# Revit family: Gira_212800
name_source: partatom
category: Elektroinstallationen
revit_build: Autodesk Revit 2017 (Build: 20160225_1515(x64)
units: mm (PartAtom-declared; Revit-internal decimal feet)

## family parameters
Basisbauteil = Fläche
Beim Laden mit Abzugskörper schneiden = Nein
Bemaßung runder Anschluss = Durchmesser verwenden
Beschriftungsausrichtung beibehalten = Nein
Gemeinsam genutzt = Nein
Raumberechnungspunkt = Nein
Teiletyp = Normal

## types (1)
- Binäreing. 8f 12 - 48 V AC/DC pot.frei KNX REG
    Anzahl der Ausgänge = 0
    Anzahl der binären Eingänge = 0
    BIM = https://media.stage.bim.site 8f.rfa
    BIMSITE_PRODUCT_ID = 7bffefd257eabbc41457cb73de1d5ba235a54360
    Beschreibung = KNX Binäreingang 8fach 12 - 48 V AC DC potenzialfrei  REG plus REG-Binäreingänge zum Anschluss von Kontakten. Die Schaltvorgänge von Kontakten (z. B. Wächter bzw. Taster) werden in KNX Telegramme umgesetzt. Die Eingänge können dabei unabhängig voneinander verschiedenen Funktionen zugeordnet oder gesperrt werden. Signalanzeige über gelbe Status-LED möglich.  Merkmale:  Jeder Eingang verfügt über den vollen Funktionsumfang. Alle kanalorientierten Funktionen lassen sich separat für jeden Eingang parametrieren.  Aktiv sendende Telegramme der Eingänge lassen sich nach Busspannungswiederkehr oder nach einem ETS-Programmiervorgang global verzögern.  Entprellzeit und Telegrammratenbegrenzung konfigurierbar.  Freie Zuordnung der Funktionen Schalten, Dimmen, Jalousie, Wertgeber und Impulszähler zu den Eingängen.  Sperrobjekt zum Sperren einzelner Eingänge (Polarität des Sperrobjekts einstellbar) für die Funktionen Schalten, Dimmen, Jalousie und Wertgeber.  Verhalten bei Busspannungswiederkehr für jeden Eingang separat parametrierbar.  Funktion Schalten: zwei unabhängige Schaltobjekte für jeden Eingang vorhanden (Schaltbefehle sind einzeln parametrierbar), Befehl bei steigender und fallender Flanke unabhängig einstellbar (EIN, AUS, UM, keine Reaktion), unabhängiges zyklisches Senden der Schaltobjekte in Abhängigkeit der Flanke oder in Abhängigkeit des Objektwerts wählbar.  Funktion Dimmen: Einflächen- und Zweiflächenbedienung, Zeit zwischen Dimmen und Schalten und Dimmschrittweite einstellbar, Telegrammwiederholung und Stopptelegramm senden möglich.  Funktion Jalousie: Befehl bei steigender Flanke einstellbar (keine Funktion, AUF, AB, UM), Bedienkonzept parametrierbar (Step - Move - Step oder Move - Step), Zeit zwischen Kurz- und Langzeitbetrieb einstellbar (nur bei Step - Move - Step), Lamellenverstellzeit einstellbar.  Funktion Wertgeber: Flanke (Taster als Schließer, Taster als Öffner, Schalter) und Wert bei Flanke parametrierbar, Wertverstellung bei Taster über langen Tastendruck für Wertgeber möglich, Lichtszenennebenstelle mit Speicherfunktion auch Speicherung der Szene ohne vorherigen Abruf möglich.  Funktion Impulszähler: Zählintervall einstellbar, Flanke (Zählen bei steigender Flanke, Zählen bei fallender Flanke, Zählen bei steigender und fallender Flanke) parametrierbar, Anzahl der erforderlichen Impulse am Eingang parametrierbar, Anzahl der erforderlichen Zählimpulse für eine Zähleränderung parametrierbar, Jeder Eingang beinhaltet einen Hauptzähler und einen Zwischenzähler, Hauptzähler und Zwischenzähler können getrennt voneinander als Vorwärts- oder Rückwärtszähler arbeiten, Start- und Endwerte der Zähler können über Parameter oder Kommunikationsobjekt vorgegeben werden, Abfrage Zählerstand über KNX oder automatisch, Verhalten nach Ablauf des Zählers ist parametrierbar, Impulszähler über KNX zurücksetzten (Zähler-Reset).  Der Binäreingang hat acht voneinander unabhängige Eingänge an die elektrische Signale im Spannungsbereich von 12 bis 48 V angeschlossen werden.  Auswertung von Gleichspannungssignale (DC) oder Wechselspannungssignale (AC).  Der Binäreingang stellt eine separate DC 24 V Hilfsspannung (SELV) für den Anschluss potenzialfreier Kontakte zur Verfügung.  Statusmeldung bei Fehler mit der Hilfsspannung auf den Bus absetzbar.  Anschluss von Zählern mit S0-Schnittstelle möglich (z. B. Energie-, Gas-, Wasserzähler).
    Blindleistung = Nein
    Breite in Teilungseinheiten = 0
    Busspannung pufferbar = Nein
    Bussystem Funkbus = Nein
    Bussystem KNX = Nein
    Bussystem KNX-Funk = Nein
    Bussystem LON = Nein
    Bussystem Powernet = Nein
    Datenblatt = https://media.stage.bim.site
    Datenblatt 1 = https://media.stage.bim.site
    GTIN = 4010337018841
    Geeignet für C-Last = Nein
    HAN = 212800
    Handschaltung = Nein
    HeinzeBIM = https://www.heinze.de
    Hersteller = Gira
    Kosten = 0 $
    Max. Anzahl der Schaltausgänge = 0
    Mit Busankopplung = Nein
    Mit LED-Anzeige = Nein
    Modulare Erweiterungsmöglichkeit = Nein
    Produktseite = https://media.stage.bim.site
    Stellgröße schaltend = Nein
    Stellgröße stetig = Nein
    Tarifumschaltung = Nein
    Typname = Binäreing. 8f 12 - 48 V AC/DC pot.frei KNX REG
    URL = https://www.gira.de
    Ventilschutzfunktion = Nein
    Verschiedene Phasen anschließbar = Nein
    Vor Ort-/Handbedienung = Nein
    Vorgabe-Ansicht = 1219 mm
    Zulassung nach PTB = Nein

## geometry (parser evidence)
native form markers: Sweep x3
no freeform markers — native parametric forms only
